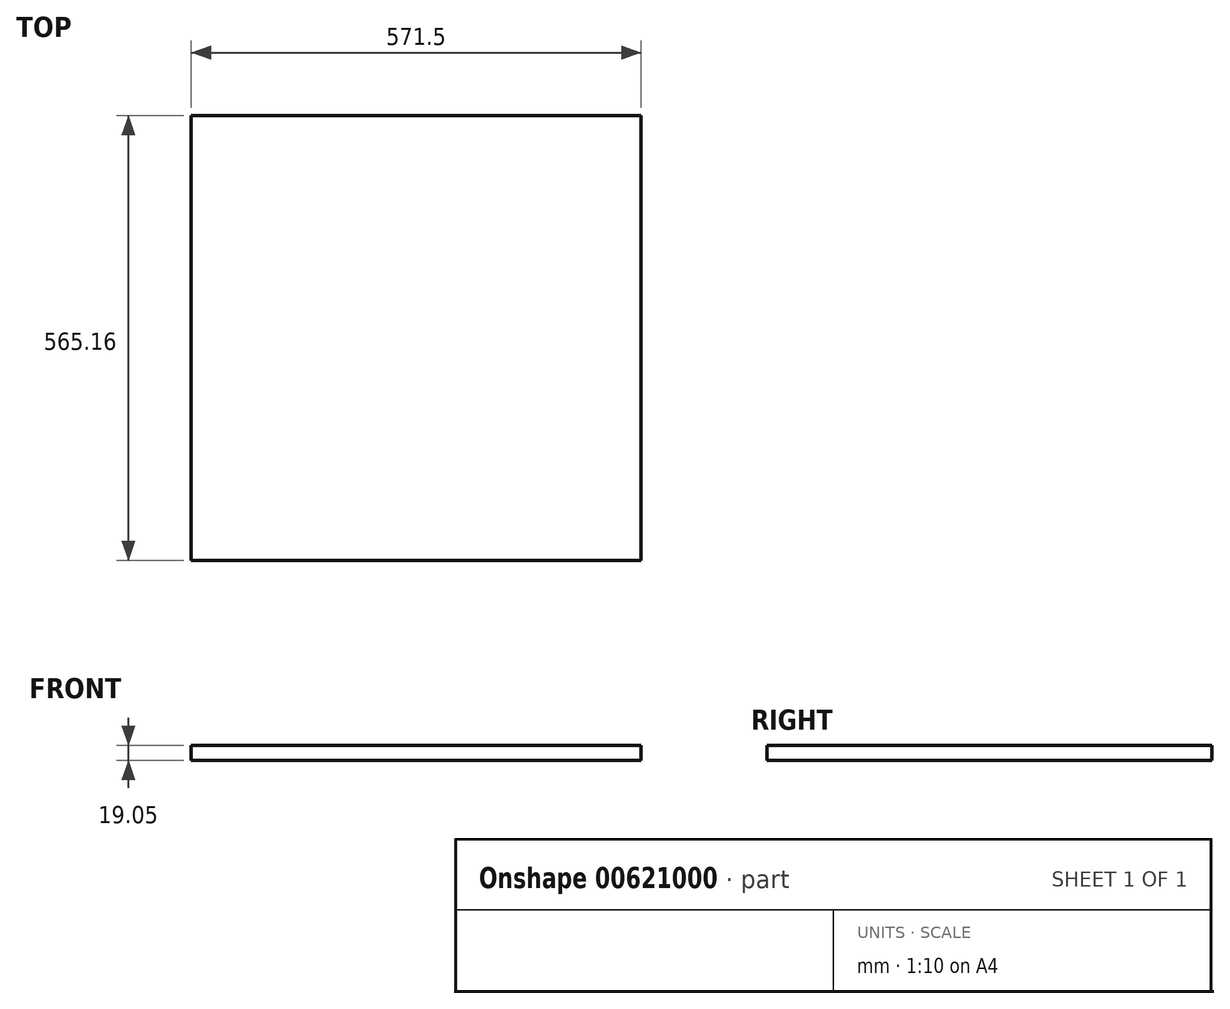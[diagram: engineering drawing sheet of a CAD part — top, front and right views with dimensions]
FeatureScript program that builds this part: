
annotation { "Feature Type Name" : "Feature", "Feature Type Description" : "" }
export const myFeature = defineFeature(function(context is Context, id is Id, definition is map)
    precondition{}
    {
        {
            var Q0;
            Q0=qCreatedBy(makeId("Top.planeOp"),FACE);
            var sketch = newSketch(context, id + "F0", { "sketchPlane" : qUnion([Q0])});
            skLineSegment(sketch, "E0.bottom", {"start": v(285.75, 282.58) * mm, "end": v(-285.75, 282.58) * mm});
            skLineSegment(sketch, "E0.top", {"start": v(285.75, -282.58) * mm, "end": v(-285.75, -282.58) * mm});
            skLineSegment(sketch, "E0.left", {"start": v(285.75, 282.58) * mm, "end": v(285.75, -282.58) * mm});
            skLineSegment(sketch, "E0.right", {"start": v(-285.75, 282.58) * mm, "end": v(-285.75, -282.58) * mm});
            skPoint(sketch, "E0.middle", {"position": v(0, 0) * mm});
            skSolve(sketch);
        }
        {
            var Q0;
            Q0=makeQuery(id+"F0.imprint","IMPRINT",FACE,{"disambiguationData":[TD([[makeQuery(id+"F0.imprint","IMPRINT",EDGE,{"derivedFrom":sQuery(id+"F0.wireOp",EDGE,"E0.bottom")}),1.0]])]});
            extrude(context, id + "F1", {"entities" : qUnion([Q0]), "depth" : 19.05 * mm, "offsetDistance" : 25.4 * mm});
        }
    });
